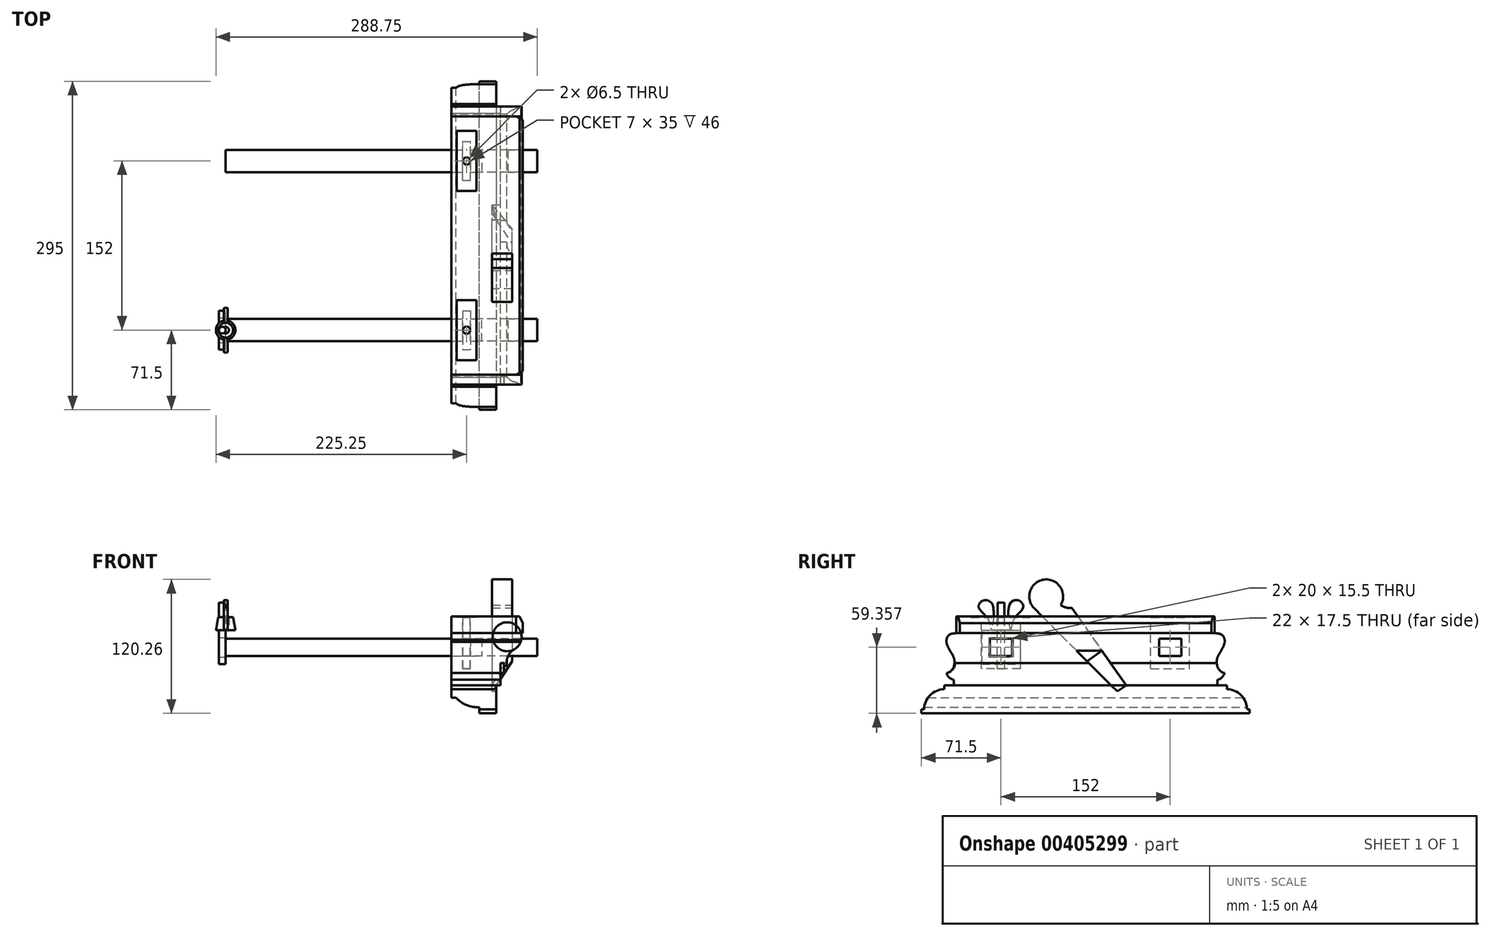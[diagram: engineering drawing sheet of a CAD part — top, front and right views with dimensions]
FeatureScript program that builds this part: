
annotation { "Feature Type Name" : "Feature", "Feature Type Description" : "" }
export const myFeature = defineFeature(function(context is Context, id is Id, definition is map)
    precondition{}
    {
        {
            var Q0;
            Q0=qCreatedBy(makeId("Front.planeOp"),FACE);
            var sketch = newSketch(context, id + "F0", { "sketchPlane" : qUnion([Q0]), "disableImprinting" : false});
            skLineSegment(sketch, "E0", {"start": v(0, 0) * mm, "end": v(0, -42.83) * mm});
            skLineSegment(sketch, "E1", {"start": v(0, -42.83) * mm, "end": v(17, -42.83) * mm});
            skLineSegment(sketch, "E2", {"start": v(17, -42.83) * mm, "end": v(17, -22.83) * mm});
            skLineSegment(sketch, "E3", {"start": v(17, -22.83) * mm, "end": v(20, -22.83) * mm});
            skLineSegment(sketch, "E4", {"start": v(20, -22.83) * mm, "end": v(20, -25.26) * mm});
            skLineSegment(sketch, "E5", {"start": v(20, -25.26) * mm, "end": v(23, -25.26) * mm});
            skLineSegment(sketch, "E6", {"start": v(23, -25.26) * mm, "end": v(35.5, 4.17) * mm});
            skLineSegment(sketch, "E7", {"start": v(35.5, 4.17) * mm, "end": v(37, 4.17) * mm});
            skLineSegment(sketch, "E8", {"start": v(37, 4.17) * mm, "end": v(37, 13.17) * mm});
            skLineSegment(sketch, "E9", {"start": v(37, 13.17) * mm, "end": v(34, 19.17) * mm});
            skLineSegment(sketch, "E10", {"start": v(34, 19.17) * mm, "end": v(0, 19.17) * mm});
            skLineSegment(sketch, "E11", {"start": v(0, 19.17) * mm, "end": v(0, 0) * mm});
            skArc(sketch, "E12", {"start": v(29.25, -10.55) * mm, "mid": v(34.9, -4.26) * mm, "end": v(35.5, 4.17) * mm});
            skArc(sketch, "E13", {"start": v(29.25, -10.55) * mm, "mid": v(23.6, -16.83) * mm, "end": v(23, -25.26) * mm});
            skLineSegment(sketch, "E14.top", {"start": v(17, -55.83) * mm, "end": v(20, -55.83) * mm});
            skLineSegment(sketch, "E14.left", {"start": v(17, -22.83) * mm, "end": v(17, -55.83) * mm});
            skLineSegment(sketch, "E14.right", {"start": v(20, -22.83) * mm, "end": v(20, -55.83) * mm});
            skSolve(sketch);
        }
        {
            var Q0;
            Q0=makeQuery(id+"F0.imprint","IMPRINT",FACE,{"disambiguationData":[TD([[makeQuery(id+"F0.imprint","IMPRINT",EDGE,{"derivedFrom":sQuery(id+"F0.wireOp",EDGE,"E0")}),1.0]])]});
            var Q1;
            {var subQ0=sQuery(id+"F0.wireOp",EDGE,"E12");Q1=makeQuery(id+"F0.imprint","IMPRINT",FACE,{"disambiguationData":[TD([[makeQuery(id+"F0.imprint","IMPRINT",EDGE,{"derivedFrom":subQ0}),1.0]])]});}
            extrude(context, id + "F1", {"entities" : qUnion([Q0, Q1]), "flatOperationType" : FlatOperationType.REMOVE, "offsetDistance" : 25 * mm, "depth" : 250 * mm, "domain" : OperationDomain.MODEL});
        }
        {
            var Q0;
            {var subQ3=sQuery(id+"F0.wireOp",EDGE,"E3");Q0=makeQuery(id+"F0.imprint","IMPRINT",FACE,{"disambiguationData":[TD([[makeQuery(id+"F0.imprint","IMPRINT",EDGE,{"derivedFrom":subQ3}),-1.0]])]});}
            extrude(context, id + "F2", {"entities" : qUnion([Q0]), "flatOperationType" : FlatOperationType.REMOVE, "offsetDistance" : 25 * mm, "depth" : 250 * mm, "domain" : OperationDomain.MODEL});
        }
        {
            var Q0;
            Q0=makeQuery(id+"F1.opExtrude","SWEPT_FACE",FACE,{"disambiguationData":[OSD([sQuery(id+"F0.wireOp",EDGE,"E0"),sQuery(id+"F0.wireOp",EDGE,"E11")])]});
            var sketch = newSketch(context, id + "F3", { "sketchPlane" : qUnion([Q0]), "disableImprinting" : false});
            skLineSegment(sketch, "E15", {"start": v(125, 19.17) * mm, "end": v(125, -42.83) * mm, "construction": true});
            skLineSegment(sketch, "E16", {"start": v(9, 19.17) * mm, "end": v(9, 4.17) * mm});
            skLineSegment(sketch, "E17", {"start": v(9, 4.17) * mm, "end": v(0, -31.83) * mm});
            skLineSegment(sketch, "E18", {"start": v(0, -31.83) * mm, "end": v(6.5, -37.83) * mm});
            skLineSegment(sketch, "E19", {"start": v(6.5, -37.83) * mm, "end": v(6.5, -42.83) * mm});
            skLineSegment(sketch, "E20", {"start": v(6.5, -42.83) * mm, "end": v(6.5, -55.83) * mm});
            skLineSegment(sketch, "E21", {"start": v(6.5, -55.83) * mm, "end": v(0, -55.83) * mm});
            skLineSegment(sketch, "E22", {"start": v(0, -55.83) * mm, "end": v(0, 19.17) * mm});
            skLineSegment(sketch, "E23", {"start": v(0, 19.17) * mm, "end": v(9, 19.17) * mm});
            skArc(sketch, "E24", {"start": v(0, -31.83) * mm, "mid": v(2.45, -35.7) * mm, "end": v(6.5, -37.83) * mm});
            skPoint(sketch, "E25.5.internal.snap0", {"position": v(4.5, -13.83) * mm});
            skFitSpline(sketch, "E25", {"points": [v(9, 4.17) * mm, v(2.4, 2.52) * mm, v(0, -3.64) * mm, v(4.5, -13.83) * mm, v(6.98, -19.62) * mm, v(6.63, -25.76) * mm, v(4.5, -29.45) * mm, v(2.76, -30.82) * mm, v(0, -31.83) * mm], "startDerivative": vector(-67.53, -10.91) * mm, "endDerivative": vector(-24.37, -5.27) * mm});
            skLineSegment(sketch, "E26.MirrorCS", {"start": v(250, -31.83) * mm, "end": v(243.5, -37.83) * mm});
            skLineSegment(sketch, "E27.MirrorCS", {"start": v(243.5, -37.83) * mm, "end": v(243.5, -42.83) * mm});
            skLineSegment(sketch, "E28.MirrorCS", {"start": v(243.5, -55.83) * mm, "end": v(250, -55.83) * mm});
            skArc(sketch, "E29.MirrorCS", {"start": v(250, -31.83) * mm, "mid": v(247.55, -35.7) * mm, "end": v(243.5, -37.83) * mm});
            skFitSpline(sketch, "E30.MirrorCS", {"points": [v(241, 4.17) * mm, v(247.6, 2.52) * mm, v(250, -3.64) * mm, v(245.5, -13.83) * mm, v(243.02, -19.62) * mm, v(243.37, -25.76) * mm, v(245.5, -29.45) * mm, v(247.24, -30.82) * mm, v(250, -31.83) * mm], "startDerivative": vector(67.53, -10.91) * mm, "endDerivative": vector(24.37, -5.27) * mm});
            skLineSegment(sketch, "E31.MirrorCS", {"start": v(241, 19.17) * mm, "end": v(241, 4.17) * mm});
            skLineSegment(sketch, "E32.MirrorCS", {"start": v(241, 4.17) * mm, "end": v(250, -31.83) * mm});
            skLineSegment(sketch, "E33.MirrorCS", {"start": v(243.5, -42.83) * mm, "end": v(243.5, -55.83) * mm});
            skLineSegment(sketch, "E34.MirrorCS", {"start": v(250, 19.17) * mm, "end": v(241, 19.17) * mm});
            skLineSegment(sketch, "E35.MirrorCS", {"start": v(250, -55.83) * mm, "end": v(250, 19.17) * mm});
            skSolve(sketch);
        }
        {
            var Q0;
            {var subQ0=sQuery(id+"F3.wireOp",EDGE,"E16");Q0=makeQuery(id+"F3.imprint","IMPRINT",FACE,{"disambiguationData":[TD([[makeQuery(id+"F3.imprint","IMPRINT",EDGE,{"derivedFrom":subQ0}),-1.0]])]});}
            var Q1;
            {var subQ0=sQuery(id+"F3.wireOp",EDGE,"E25");var subQ1=sQuery(id+"F3.wireOp",EDGE,"E17");var subQ3=makeQuery(id+"F3.imprint","INTERSECT",VERTEX,{"derivedFrom":[subQ1,subQ0]});Q1=makeQuery(id+"F3.imprint","IMPRINT",FACE,{"disambiguationData":[TD([[makeQuery(id+"F3.imprint","IMPRINT",EDGE,{"disambiguationData":[TD([[subQ3,-1.0]])],"derivedFrom":subQ1}),1.0]])]});}
            var Q2;
            {var subQ0=sQuery(id+"F3.wireOp",EDGE,"E25");var subQ1=sQuery(id+"F3.wireOp",EDGE,"E22");var subQ5=makeQuery(id+"F3.imprint","INTERSECT",VERTEX,{"disambiguationData":[OD(1.0)],"derivedFrom":[subQ1,subQ0]});Q2=makeQuery(id+"F3.imprint","IMPRINT",FACE,{"disambiguationData":[TD([[makeQuery(id+"F3.imprint","IMPRINT",EDGE,{"disambiguationData":[TD([[subQ5,-1.0]])],"derivedFrom":subQ0}),-1.0]])]});}
            var Q3;
            {var subQ0=sQuery(id+"F3.wireOp",EDGE,"E19");Q3=makeQuery(id+"F3.imprint","IMPRINT",FACE,{"disambiguationData":[TD([[makeQuery(id+"F3.imprint","IMPRINT",EDGE,{"derivedFrom":subQ0}),-1.0]])]});}
            var Q4;
            {var subQ0=sQuery(id+"F3.wireOp",EDGE,"E20");Q4=makeQuery(id+"F3.imprint","IMPRINT",FACE,{"disambiguationData":[TD([[makeQuery(id+"F3.imprint","IMPRINT",EDGE,{"derivedFrom":subQ0}),-1.0]])]});}
            var Q5;
            {var subQ0=sQuery(id+"F3.wireOp",EDGE,"E31.MirrorCS");Q5=makeQuery(id+"F3.imprint","IMPRINT",FACE,{"disambiguationData":[TD([[makeQuery(id+"F3.imprint","IMPRINT",EDGE,{"derivedFrom":subQ0}),1.0]])]});}
            var Q6;
            {var subQ0=sQuery(id+"F3.wireOp",EDGE,"E35.MirrorCS");var subQ1=sQuery(id+"F3.wireOp",EDGE,"E30.MirrorCS");var subQ2=makeQuery(id+"F3.imprint","INTERSECT",VERTEX,{"disambiguationData":[OD(1.0)],"derivedFrom":[subQ1,subQ0]});Q6=makeQuery(id+"F3.imprint","IMPRINT",FACE,{"disambiguationData":[TD([[makeQuery(id+"F3.imprint","IMPRINT",EDGE,{"disambiguationData":[TD([[subQ2,-1.0]])],"derivedFrom":subQ1}),1.0]])]});}
            var Q7;
            {var subQ0=sQuery(id+"F3.wireOp",EDGE,"E32.MirrorCS");var subQ1=sQuery(id+"F3.wireOp",EDGE,"E30.MirrorCS");var subQ3=makeQuery(id+"F3.imprint","INTERSECT",VERTEX,{"derivedFrom":[subQ1,subQ0]});Q7=makeQuery(id+"F3.imprint","IMPRINT",FACE,{"disambiguationData":[TD([[makeQuery(id+"F3.imprint","IMPRINT",EDGE,{"disambiguationData":[TD([[subQ3,-1.0]])],"derivedFrom":subQ1}),1.0]])]});}
            var Q8;
            {var subQ0=sQuery(id+"F3.wireOp",EDGE,"E27.MirrorCS");Q8=makeQuery(id+"F3.imprint","IMPRINT",FACE,{"disambiguationData":[TD([[makeQuery(id+"F3.imprint","IMPRINT",EDGE,{"derivedFrom":subQ0}),1.0]])]});}
            var Q9;
            {var subQ0=sQuery(id+"F3.wireOp",EDGE,"E28.MirrorCS");Q9=makeQuery(id+"F3.imprint","IMPRINT",FACE,{"disambiguationData":[TD([[makeQuery(id+"F3.imprint","IMPRINT",EDGE,{"derivedFrom":subQ0}),1.0]])]});}
            extrude(context, id + "F4", {"entities" : qUnion([Q0, Q1, Q2, Q3, Q4, Q5, Q6, Q7, Q8, Q9]), "operationType" : NewBodyOperationType.REMOVE, "endBound" : BoundingType.THROUGH_ALL, "oppositeDirection" : true, "depth" : 25 * mm});
        }
        {
            var Q0;
            Q0=makeQuery(id+"F2.opExtrude","SWEPT_FACE",FACE,{"disambiguationData":[OSD([sQuery(id+"F0.wireOp",EDGE,"E14.left")])]});
            var sketch = newSketch(context, id + "F5", { "sketchPlane" : qUnion([Q0])});
            skFitSpline(sketch, "E36.0", {"points": [v(0, -31.83) * mm, v(0.74, -31.67) * mm, v(2.94, -30.89) * mm, v(4.62, -29.53) * mm, v(7.17, -25.8) * mm, v(7.43, -19.25) * mm, v(4.68, -13.85) * mm, v(-1.65, -4.08) * mm, v(2, 3.76) * mm, v(5.87, 3.66) * mm, v(9, 4.17) * mm]});
            skArc(sketch, "E37.0", {"start": v(6.5, -37.83) * mm, "mid": v(2.45, -35.7) * mm, "end": v(0, -31.83) * mm});
            skLineSegment(sketch, "E38.0", {"start": v(6.5, -42.83) * mm, "end": v(6.5, -37.83) * mm});
            skLineSegment(sketch, "E39", {"start": v(7.16, -22.83) * mm, "end": v(0, -22.83) * mm});
            skLineSegment(sketch, "E40", {"start": v(0, -22.83) * mm, "end": v(0, -55.83) * mm});
            skLineSegment(sketch, "E41", {"start": v(0, -55.83) * mm, "end": v(6.5, -55.83) * mm});
            skLineSegment(sketch, "E42", {"start": v(6.5, -55.83) * mm, "end": v(6.5, -42.83) * mm});
            skLineSegment(sketch, "E43", {"start": v(125, -22.83) * mm, "end": v(125, -55.83) * mm, "construction": true});
            skLineSegment(sketch, "E44.MirrorCS", {"start": v(243.5, -42.83) * mm, "end": v(243.5, -37.83) * mm});
            skLineSegment(sketch, "E45.MirrorCS", {"start": v(242.84, -22.83) * mm, "end": v(250, -22.83) * mm});
            skLineSegment(sketch, "E46.MirrorCS", {"start": v(250, -55.83) * mm, "end": v(243.5, -55.83) * mm});
            skArc(sketch, "E47.MirrorCS", {"start": v(243.5, -37.83) * mm, "mid": v(247.55, -35.7) * mm, "end": v(250, -31.83) * mm});
            skLineSegment(sketch, "E48.MirrorCS", {"start": v(243.5, -55.83) * mm, "end": v(243.5, -42.83) * mm});
            skLineSegment(sketch, "E49.MirrorCS", {"start": v(250, -22.83) * mm, "end": v(250, -55.83) * mm});
            skFitSpline(sketch, "E50.0", {"points": [v(250, -31.83) * mm, v(249.26, -31.67) * mm, v(247.06, -30.89) * mm, v(245.38, -29.53) * mm, v(242.83, -25.8) * mm, v(242.57, -19.25) * mm, v(245.32, -13.85) * mm, v(251.65, -4.08) * mm, v(248, 3.76) * mm, v(244.13, 3.66) * mm, v(241, 4.17) * mm]});
            skSolve(sketch);
        }
        {
            var Q0;
            {var subQ0=sQuery(id+"F5.wireOp",EDGE,"E45.MirrorCS");Q0=makeQuery(id+"F5.imprint","IMPRINT",FACE,{"disambiguationData":[TD([[makeQuery(id+"F5.imprint","IMPRINT",EDGE,{"derivedFrom":subQ0}),1.0]])]});}
            var Q1;
            Q1=makeQuery(id+"F5.imprint","IMPRINT",FACE,{"disambiguationData":[TD([[makeQuery(id+"F5.imprint","IMPRINT",EDGE,{"derivedFrom":sQuery(id+"F5.wireOp",EDGE,"E44.MirrorCS")}),-1.0]])]});
            var Q2;
            {var subQ0=sQuery(id+"F5.wireOp",EDGE,"E36.0");Q2=makeQuery(id+"F5.imprint","IMPRINT",FACE,{"disambiguationData":[TD([[makeQuery(id+"F5.imprint","IMPRINT",EDGE,{"derivedFrom":subQ0}),1.0]])]});}
            var Q3;
            {var subQ2=sQuery(id+"F5.wireOp",EDGE,"E37.0");Q3=makeQuery(id+"F5.imprint","IMPRINT",FACE,{"disambiguationData":[TD([[makeQuery(id+"F5.imprint","IMPRINT",EDGE,{"derivedFrom":subQ2}),1.0]])]});}
            extrude(context, id + "F6", {"entities" : qUnion([Q0, Q1, Q2, Q3]), "operationType" : NewBodyOperationType.REMOVE, "endBound" : BoundingType.THROUGH_ALL, "oppositeDirection" : true, "depth" : 25 * mm});
        }
        {
            var Q0;
            Q0=makeQuery(id+"F1.opExtrude","SWEPT_FACE",FACE,{"disambiguationData":[OSD([sQuery(id+"F0.wireOp",EDGE,"E10")])]});
            var sketch = newSketch(context, id + "F7", { "sketchPlane" : qUnion([Q0])});
            skLineSegment(sketch, "E51", {"start": v(34, -9) * mm, "end": v(31, -9) * mm});
            skLineSegment(sketch, "E52", {"start": v(31, -9) * mm, "end": v(37, -12) * mm});
            skLineSegment(sketch, "E53", {"start": v(37, -12) * mm, "end": v(37, -9) * mm});
            skLineSegment(sketch, "E54", {"start": v(37, -9) * mm, "end": v(34, -9) * mm});
            skLineSegment(sketch, "E55", {"start": v(0, -125) * mm, "end": v(34, -125) * mm, "construction": true});
            skLineSegment(sketch, "E56.MirrorCS", {"start": v(37, -238) * mm, "end": v(37, -241) * mm});
            skLineSegment(sketch, "E57.MirrorCS", {"start": v(31, -241) * mm, "end": v(37, -238) * mm});
            skLineSegment(sketch, "E58.MirrorCS", {"start": v(34, -241) * mm, "end": v(31, -241) * mm});
            skLineSegment(sketch, "E59.MirrorCS", {"start": v(37, -241) * mm, "end": v(34, -241) * mm});
            skSolve(sketch);
        }
        {
            var Q0;
            {var subQ0=sQuery(id+"F7.wireOp",EDGE,"E51");Q0=makeQuery(id+"F7.imprint","IMPRINT",FACE,{"disambiguationData":[TD([[makeQuery(id+"F7.imprint","IMPRINT",EDGE,{"derivedFrom":subQ0}),1.0]])]});}
            var Q1;
            {var subQ0=sQuery(id+"F7.wireOp",EDGE,"E53");Q1=makeQuery(id+"F7.imprint","IMPRINT",FACE,{"disambiguationData":[TD([[makeQuery(id+"F7.imprint","IMPRINT",EDGE,{"derivedFrom":subQ0}),1.0]])]});}
            var Q2;
            Q2=makeQuery(id+"F1.opExtrude","SWEPT_FACE",FACE,{"disambiguationData":[OSD([sQuery(id+"F0.wireOp",EDGE,"E7")])]});
            extrude(context, id + "F8", {"entities" : qUnion([Q0, Q1]), "operationType" : NewBodyOperationType.REMOVE, "endBound" : BoundingType.UP_TO_SURFACE, "oppositeDirection" : true, "endBoundEntityFace" : qUnion([Q2]), "depth" : 25 * mm});
        }
        {
            var Q0;
            {var subQ0=sQuery(id+"F7.wireOp",EDGE,"E56.MirrorCS");Q0=makeQuery(id+"F7.imprint","IMPRINT",FACE,{"disambiguationData":[TD([[makeQuery(id+"F7.imprint","IMPRINT",EDGE,{"derivedFrom":subQ0}),-1.0]])]});}
            var Q1;
            {var subQ0=sQuery(id+"F7.wireOp",EDGE,"E58.MirrorCS");Q1=makeQuery(id+"F7.imprint","IMPRINT",FACE,{"disambiguationData":[TD([[makeQuery(id+"F7.imprint","IMPRINT",EDGE,{"derivedFrom":subQ0}),-1.0]])]});}
            var Q2;
            Q2=makeQuery(id+"F1.opExtrude","SWEPT_FACE",FACE,{"disambiguationData":[OSD([sQuery(id+"F0.wireOp",EDGE,"E7")])]});
            extrude(context, id + "F9", {"entities" : qUnion([Q0, Q1]), "operationType" : NewBodyOperationType.REMOVE, "endBound" : BoundingType.UP_TO_SURFACE, "oppositeDirection" : true, "endBoundEntityFace" : qUnion([Q2]), "depth" : 25 * mm});
        }
        {
            var Q0;
            Q0=makeQuery(id+"F1.opExtrude","SWEPT_FACE",FACE,{"disambiguationData":[OSD([sQuery(id+"F0.wireOp",EDGE,"E0"),sQuery(id+"F0.wireOp",EDGE,"E11")])]});
            var sketch = newSketch(context, id + "F10", { "sketchPlane" : qUnion([Q0])});
            skLineSegment(sketch, "E60.bottom", {"start": v(39, -0.83) * mm, "end": v(59, -0.83) * mm});
            skLineSegment(sketch, "E60.top", {"start": v(39, -16.33) * mm, "end": v(59, -16.33) * mm});
            skLineSegment(sketch, "E60.left", {"start": v(39, -0.83) * mm, "end": v(39, -16.33) * mm});
            skLineSegment(sketch, "E60.right", {"start": v(59, -0.83) * mm, "end": v(59, -16.33) * mm});
            skLineSegment(sketch, "E61", {"start": v(125, 19.17) * mm, "end": v(125, -42.83) * mm, "construction": true});
            skLineSegment(sketch, "E62.MirrorCS", {"start": v(211, -0.83) * mm, "end": v(191, -0.83) * mm});
            skLineSegment(sketch, "E63.MirrorCS", {"start": v(211, -16.33) * mm, "end": v(191, -16.33) * mm});
            skLineSegment(sketch, "E64.MirrorCS", {"start": v(211, -0.83) * mm, "end": v(211, -16.33) * mm});
            skLineSegment(sketch, "E65.MirrorCS", {"start": v(191, -0.83) * mm, "end": v(191, -16.33) * mm});
            skSolve(sketch);
        }
        {
            var Q0;
            Q0=makeQuery(id+"F10.imprint","IMPRINT",FACE,{"disambiguationData":[TD([[makeQuery(id+"F10.imprint","IMPRINT",EDGE,{"derivedFrom":sQuery(id+"F10.wireOp",EDGE,"E60.bottom")}),-1.0]])]});
            var Q1;
            Q1=makeQuery(id+"F10.imprint","IMPRINT",FACE,{"disambiguationData":[TD([[makeQuery(id+"F10.imprint","IMPRINT",EDGE,{"derivedFrom":sQuery(id+"F10.wireOp",EDGE,"E62.MirrorCS")}),1.0]])]});
            var Q2;
            Q2=makeQuery(id+"F1.opExtrude","SWEPT_FACE",FACE,{"disambiguationData":[OSD([sQuery(id+"F0.wireOp",EDGE,"E12")])]});
            extrude(context, id + "F11", {"entities" : qUnion([Q0, Q1]), "operationType" : NewBodyOperationType.REMOVE, "endBound" : BoundingType.UP_TO_NEXT, "oppositeDirection" : true, "endBoundEntityFace" : qUnion([Q2]), "depth" : 25 * mm});
        }
        {
            var Q0;
            Q0=makeQuery(id+"F10.imprint","IMPRINT",FACE,{"disambiguationData":[TD([[makeQuery(id+"F10.imprint","IMPRINT",EDGE,{"derivedFrom":sQuery(id+"F10.wireOp",EDGE,"E62.MirrorCS")}),1.0]])]});
            var Q1;
            Q1=makeQuery(id+"F10.imprint","IMPRINT",FACE,{"disambiguationData":[TD([[makeQuery(id+"F10.imprint","IMPRINT",EDGE,{"derivedFrom":sQuery(id+"F10.wireOp",EDGE,"E60.bottom")}),-1.0]])]});
            var Q2;
            Q2=makeQuery(id+"F1.opExtrude","SWEPT_FACE",FACE,{"disambiguationData":[OSD([sQuery(id+"F0.wireOp",EDGE,"E13")])]});
            extrude(context, id + "F12", {"entities" : qUnion([Q0, Q1]), "oppositeDirection" : true, "endBoundEntityFace" : qUnion([Q2]), "depth" : 50 * mm});
        }
        {
            var Q0;
            Q0=makeQuery(id+"F10.imprint","IMPRINT",FACE,{"disambiguationData":[TD([[makeQuery(id+"F10.imprint","IMPRINT",EDGE,{"derivedFrom":sQuery(id+"F10.wireOp",EDGE,"E62.MirrorCS")}),1.0]])]});
            var Q1;
            Q1=makeQuery(id+"F10.imprint","IMPRINT",FACE,{"disambiguationData":[TD([[makeQuery(id+"F10.imprint","IMPRINT",EDGE,{"derivedFrom":sQuery(id+"F10.wireOp",EDGE,"E60.bottom")}),-1.0]])]});
            extrude(context, id + "F13", {"entities" : qUnion([Q0, Q1]), "depth" : 230 * mm});
        }
        {
            var Q0;
            Q0=makeQuery(id+"F12.opExtrude","SWEPT_FACE",FACE,{"disambiguationData":[OSD([sQuery(id+"F10.wireOp",EDGE,"E60.left")])]});
            var sketch = newSketch(context, id + "F14", { "sketchPlane" : qUnion([Q0])});
            skArc(sketch, "E66.0", {"start": v(-29.25, -10.55) * mm, "mid": v(-33.7, -6.47) * mm, "end": v(-35.83, -0.83) * mm});
            skArc(sketch, "E67.0", {"start": v(-29.25, -10.55) * mm, "mid": v(-26.08, -13.01) * mm, "end": v(-23.82, -16.33) * mm});
            skLineSegment(sketch, "E68.0", {"start": v(-50, -16.33) * mm, "end": v(0, -16.33) * mm});
            skLineSegment(sketch, "E69.0", {"start": v(-50, -0.83) * mm, "end": v(-50, -16.33) * mm});
            skLineSegment(sketch, "E70.0", {"start": v(-50, -0.83) * mm, "end": v(0, -0.83) * mm});
            skSolve(sketch);
        }
        {
            var Q0;
            {var subQ3=sQuery(id+"F14.wireOp",EDGE,"E66.0");Q0=makeQuery(id+"F14.imprint","IMPRINT",FACE,{"disambiguationData":[TD([[makeQuery(id+"F14.imprint","IMPRINT",EDGE,{"derivedFrom":subQ3}),1.0]])]});}
            var Q1;
            Q1=makeQuery(id+"F12.opExtrude","SWEPT_FACE",FACE,{"disambiguationData":[OSD([sQuery(id+"F10.wireOp",EDGE,"E60.right")])]});
            extrude(context, id + "F15", {"entities" : qUnion([Q0]), "operationType" : NewBodyOperationType.REMOVE, "endBound" : BoundingType.UP_TO_SURFACE, "oppositeDirection" : true, "endBoundEntityFace" : qUnion([Q1]), "depth" : 25 * mm});
        }
        {
            var Q0;
            Q0=makeQuery(id+"F12.opExtrude","SWEPT_FACE",FACE,{"disambiguationData":[OSD([sQuery(id+"F10.wireOp",EDGE,"E65.MirrorCS")])]});
            var sketch = newSketch(context, id + "F16", { "sketchPlane" : qUnion([Q0])});
            skArc(sketch, "E71.0", {"start": v(-29.25, -10.55) * mm, "mid": v(-33.7, -6.47) * mm, "end": v(-35.83, -0.83) * mm});
            skArc(sketch, "E72.0", {"start": v(-29.25, -10.55) * mm, "mid": v(-26.08, -13.01) * mm, "end": v(-23.82, -16.33) * mm});
            skLineSegment(sketch, "E73.0", {"start": v(-50, -16.33) * mm, "end": v(0, -16.33) * mm});
            skLineSegment(sketch, "E74.0", {"start": v(-50, -0.83) * mm, "end": v(-50, -16.33) * mm});
            skLineSegment(sketch, "E75.0", {"start": v(-50, -0.83) * mm, "end": v(0, -0.83) * mm});
            skSolve(sketch);
        }
        {
            var Q0;
            {var subQ3=sQuery(id+"F16.wireOp",EDGE,"E71.0");Q0=makeQuery(id+"F16.imprint","IMPRINT",FACE,{"disambiguationData":[TD([[makeQuery(id+"F16.imprint","IMPRINT",EDGE,{"derivedFrom":subQ3}),1.0]])]});}
            var Q1;
            Q1=makeQuery(id+"F12.opExtrude","SWEPT_FACE",FACE,{"disambiguationData":[OSD([sQuery(id+"F10.wireOp",EDGE,"E64.MirrorCS")])]});
            extrude(context, id + "F17", {"entities" : qUnion([Q0]), "operationType" : NewBodyOperationType.REMOVE, "endBound" : BoundingType.UP_TO_SURFACE, "oppositeDirection" : true, "endBoundEntityFace" : qUnion([Q1]), "depth" : 25 * mm});
        }
        {
            var Q0;
            Q0=makeQuery(id+"F13.opExtrude","SWEPT_BODY",BODY,{"disambiguationData":[OSD([sQuery(id+"F10.wireOp",EDGE,"E62.MirrorCS"),sQuery(id+"F10.wireOp",EDGE,"E63.MirrorCS"),sQuery(id+"F10.wireOp",EDGE,"E64.MirrorCS"),sQuery(id+"F10.wireOp",EDGE,"E65.MirrorCS")])]});
            var Q1;
            Q1=makeQuery(id+"F12.opExtrude","SWEPT_BODY",BODY,{"disambiguationData":[OSD([sQuery(id+"F10.wireOp",EDGE,"E62.MirrorCS"),sQuery(id+"F10.wireOp",EDGE,"E63.MirrorCS"),sQuery(id+"F10.wireOp",EDGE,"E64.MirrorCS"),sQuery(id+"F10.wireOp",EDGE,"E65.MirrorCS")])]});
            booleanBodies(context, id + "F18", {"operationType" : BooleanOperationType.UNION, "tools" : qUnion([Q0, Q1])});
        }
        {
            var Q0;
            Q0=makeQuery(id+"F1.opExtrude","SWEPT_FACE",FACE,{"disambiguationData":[OSD([sQuery(id+"F0.wireOp",EDGE,"E0"),sQuery(id+"F0.wireOp",EDGE,"E11")])]});
            cPlane(context, id + "F19", {"entities" : qUnion([Q0]), "cplaneType" : CPlaneType.OFFSET, "offset" : 18.5 * mm, "oppositeDirection" : true, "width" : 150 * mm, "height" : 150 * mm});
        }
        {
            var Q0;
            Q0=qCreatedBy(id+"F19.planeOp",FACE);
            var sketch = newSketch(context, id + "F20", { "sketchPlane" : qUnion([Q0])});
            skLineSegment(sketch, "E76.0", {"start": v(241, 19.17) * mm, "end": v(9, 19.17) * mm});
            skLineSegment(sketch, "E77.0", {"start": v(243.5, -55.83) * mm, "end": v(6.5, -55.83) * mm});
            skLineSegment(sketch, "E78", {"start": v(164, 19.17) * mm, "end": v(89, -55.83) * mm});
            skLineSegment(sketch, "E79", {"start": v(132, 19.17) * mm, "end": v(79.48, -55.83) * mm});
            skLineSegment(sketch, "E80", {"start": v(132, 19.17) * mm, "end": v(137.36, 26.82) * mm});
            skArc(sketch, "E81", {"start": v(137.36, 26.82) * mm, "mid": v(142.56, 27.1) * mm, "end": v(147.35, 29.16) * mm});
            skLineSegment(sketch, "E82", {"start": v(164, 19.17) * mm, "end": v(171.14, 26.3) * mm});
            skArc(sketch, "E83", {"start": v(171.14, 26.3) * mm, "mid": v(162.18, 52.2) * mm, "end": v(147.35, 29.16) * mm});
            skLineSegment(sketch, "E84", {"start": v(88.59, -42.83) * mm, "end": v(102, -42.83) * mm});
            skSolve(sketch);
        }
        {
            var Q0;
            {var subQ0=sQuery(id+"F20.wireOp",EDGE,"E78");Q0=makeQuery(id+"F20.imprint","IMPRINT",FACE,{"disambiguationData":[TD([[makeQuery(id+"F20.imprint","IMPRINT",EDGE,{"derivedFrom":subQ0}),-1.0]])]});}
            extrude(context, id + "F21", {"entities" : qUnion([Q0]), "operationType" : NewBodyOperationType.REMOVE, "oppositeDirection" : true, "depth" : 18 * mm, "symmetric" : true});
        }
        {
            var Q0;
            Q0=makeQuery(id+"F1.opExtrude","SWEPT_FACE",FACE,{"disambiguationData":[OSD([sQuery(id+"F0.wireOp",EDGE,"E0"),sQuery(id+"F0.wireOp",EDGE,"E11")])]});
            extrude(context, id + "F22", {"entities" : qUnion([Q0]), "depth" : 27 * mm});
        }
        {
            var Q0;
            Q0=makeQuery(id+"F22.opExtrude","CAP_FACE",FACE,{"disambiguationData":[OSD([sQuery(id+"F0.wireOp",EDGE,"E0"),sQuery(id+"F0.wireOp",EDGE,"E11")])],"isStart":false});
            var sketch = newSketch(context, id + "F23", { "sketchPlane" : qUnion([Q0])});
            skLineSegment(sketch, "E85", {"start": v(6.5, -42.83) * mm, "end": v(-2, -42.83) * mm});
            skLineSegment(sketch, "E86", {"start": v(-2, -42.83) * mm, "end": v(-2, -46.33) * mm});
            skLineSegment(sketch, "E87", {"start": v(-20, -64.33) * mm, "end": v(-22.5, -64.33) * mm});
            skLineSegment(sketch, "E88", {"start": v(-22.5, -64.33) * mm, "end": v(-22.5, -67.94) * mm});
            skArc(sketch, "E89", {"start": v(-2, -46.33) * mm, "mid": v(-14.73, -51.6) * mm, "end": v(-20, -64.33) * mm});
            skLineSegment(sketch, "E90", {"start": v(125, 19.17) * mm, "end": v(125, -42.83) * mm, "construction": true});
            skLineSegment(sketch, "E91.MirrorCS", {"start": v(270, -64.33) * mm, "end": v(272.5, -64.33) * mm});
            skLineSegment(sketch, "E92.MirrorCS", {"start": v(252, -42.83) * mm, "end": v(252, -46.33) * mm});
            skLineSegment(sketch, "E93.MirrorCS", {"start": v(243.5, -42.83) * mm, "end": v(252, -42.83) * mm});
            skArc(sketch, "E94.MirrorCS", {"start": v(252, -46.33) * mm, "mid": v(264.73, -51.6) * mm, "end": v(270, -64.33) * mm});
            skLineSegment(sketch, "E95.MirrorCS", {"start": v(272.5, -64.33) * mm, "end": v(272.5, -67.94) * mm});
            skLineSegment(sketch, "E96", {"start": v(-22.5, -67.94) * mm, "end": v(272.5, -67.94) * mm});
            skLineSegment(sketch, "E97", {"start": v(243.5, -42.83) * mm, "end": v(6.5, -42.83) * mm});
            skSolve(sketch);
        }
        {
            var Q0;
            Q0=makeQuery(id+"F23.imprint","IMPRINT",FACE,{"disambiguationData":[TD([[makeQuery(id+"F23.imprint","IMPRINT",EDGE,{"derivedFrom":sQuery(id+"F23.wireOp",EDGE,"E85")}),1.0]])]});
            extrude(context, id + "F24", {"entities" : qUnion([Q0]), "operationType" : NewBodyOperationType.ADD, "oppositeDirection" : true, "depth" : 40 * mm});
        }
        {
            var Q0;
            Q0=makeQuery(id+"F24.opExtrude","SWEPT_FACE",FACE,{"disambiguationData":[OSD([sQuery(id+"F23.wireOp",EDGE,"E88")])]});
            var sketch = newSketch(context, id + "F25", { "sketchPlane" : qUnion([Q0])});
            skLineSegment(sketch, "E98", {"start": v(2, -67.94) * mm, "end": v(2, -62.44) * mm});
            skLineSegment(sketch, "E99", {"start": v(23, -53.94) * mm, "end": v(27, -53.94) * mm});
            skLineSegment(sketch, "E100", {"start": v(2, -67.94) * mm, "end": v(27, -67.94) * mm});
            skLineSegment(sketch, "E101", {"start": v(27, -67.94) * mm, "end": v(27, -53.94) * mm});
            skArc(sketch, "E102", {"start": v(2, -62.44) * mm, "mid": v(13.47, -60.6) * mm, "end": v(23, -53.94) * mm});
            skSolve(sketch);
        }
        {
            var Q0;
            {var subQ3=sQuery(id+"F25.wireOp",EDGE,"E99");Q0=makeQuery(id+"F25.imprint","IMPRINT",FACE,{"disambiguationData":[TD([[makeQuery(id+"F25.imprint","IMPRINT",EDGE,{"derivedFrom":subQ3}),-1.0]])]});}
            var Q1;
            {var subQ0=sQuery(id+"F25.wireOp",EDGE,"E100");Q1=makeQuery(id+"F25.imprint","IMPRINT",FACE,{"disambiguationData":[TD([[makeQuery(id+"F25.imprint","IMPRINT",EDGE,{"derivedFrom":subQ0}),1.0]])]});}
            extrude(context, id + "F26", {"entities" : qUnion([Q0, Q1]), "operationType" : NewBodyOperationType.REMOVE, "endBound" : BoundingType.THROUGH_ALL, "oppositeDirection" : true, "depth" : 25 * mm});
        }
        {
            var Q0;
            {var subQ5=sQuery(id+"F20.wireOp",EDGE,"E84");Q0=makeQuery(id+"F20.imprint","IMPRINT",FACE,{"disambiguationData":[TD([[makeQuery(id+"F20.imprint","IMPRINT",EDGE,{"derivedFrom":subQ5}),1.0]])]});}
            var Q1;
            {var subQ1=sQuery(id+"F20.wireOp",EDGE,"E80");Q1=makeQuery(id+"F20.imprint","IMPRINT",FACE,{"disambiguationData":[TD([[makeQuery(id+"F20.imprint","IMPRINT",EDGE,{"derivedFrom":subQ1}),-1.0]])]});}
            extrude(context, id + "F27", {"entities" : qUnion([Q0, Q1]), "depth" : 18 * mm, "symmetric" : true});
        }
        {
            var Q0;
            Q0=makeQuery(id+"F27.opExtrude","SWEPT_FACE",FACE,{"disambiguationData":[OSD([sQuery(id+"F20.wireOp",EDGE,"E79"),sQuery(id+"F20.wireOp",EDGE,"E80")])]});
            var sketch = newSketch(context, id + "F28", { "sketchPlane" : qUnion([Q0])});
            skLineSegment(sketch, "E103", {"start": v(-9.5, 15.72) * mm, "end": v(-27.5, 53.72) * mm});
            skLineSegment(sketch, "E104", {"start": v(-27.5, 53.72) * mm, "end": v(-27.5, 15.72) * mm});
            skLineSegment(sketch, "E105", {"start": v(-27.5, 15.72) * mm, "end": v(-9.5, 15.72) * mm});
            skSolve(sketch);
        }
        {
            var Q0;
            Q0=makeQuery(id+"F28.imprint","IMPRINT",FACE,{"disambiguationData":[TD([[makeQuery(id+"F28.imprint","IMPRINT",EDGE,{"derivedFrom":sQuery(id+"F28.wireOp",EDGE,"E103")}),1.0]])]});
            var Q1;
            Q1=makeQuery(id+"F27.opExtrude","SWEPT_FACE",FACE,{"disambiguationData":[OSD([sQuery(id+"F20.wireOp",EDGE,"E78"),sQuery(id+"F20.wireOp",EDGE,"E82")])]});
            extrude(context, id + "F29", {"entities" : qUnion([Q0]), "operationType" : NewBodyOperationType.REMOVE, "endBound" : BoundingType.UP_TO_SURFACE, "oppositeDirection" : true, "endBoundEntityFace" : qUnion([Q1]), "depth" : 25 * mm});
        }
        {
            var Q0;
            Q0=makeQuery(id+"F22.opExtrude","SWEPT_FACE",FACE,{"disambiguationData":[OSD([sQuery(id+"F0.wireOp",EDGE,"E10"),sQuery(id+"F0.wireOp",EDGE,"E11")])]});
            var sketch = newSketch(context, id + "F30", { "sketchPlane" : qUnion([Q0])});
            skLineSegment(sketch, "E106", {"start": v(0, -125) * mm, "end": v(-27, -125) * mm, "construction": true});
            skLineSegment(sketch, "E107.bottom", {"start": v(-4.5, -22) * mm, "end": v(-22.5, -22) * mm});
            skLineSegment(sketch, "E107.top", {"start": v(-4.5, -76) * mm, "end": v(-22.5, -76) * mm});
            skLineSegment(sketch, "E107.left", {"start": v(-4.5, -22) * mm, "end": v(-4.5, -76) * mm});
            skLineSegment(sketch, "E107.right", {"start": v(-22.5, -22) * mm, "end": v(-22.5, -76) * mm});
            skLineSegment(sketch, "E108", {"start": v(-4.5, -49) * mm, "end": v(-22.5, -49) * mm, "construction": true});
            skLineSegment(sketch, "E109", {"start": v(-4.5, -22) * mm, "end": v(0, -22) * mm, "construction": true});
            skLineSegment(sketch, "E110", {"start": v(-22.5, -22) * mm, "end": v(-27, -22) * mm, "construction": true});
            skLineSegment(sketch, "E111.bottom", {"start": v(-17, -66.5) * mm, "end": v(-10, -66.5) * mm});
            skLineSegment(sketch, "E111.top", {"start": v(-17, -31.5) * mm, "end": v(-10, -31.5) * mm});
            skLineSegment(sketch, "E111.left", {"start": v(-17, -66.5) * mm, "end": v(-17, -31.5) * mm});
            skLineSegment(sketch, "E111.right", {"start": v(-10, -66.5) * mm, "end": v(-10, -31.5) * mm});
            skPoint(sketch, "E111.middle", {"position": v(-13.5, -49) * mm});
            skLineSegment(sketch, "E112.MirrorCS", {"start": v(-4.5, -228) * mm, "end": v(0, -228) * mm, "construction": true});
            skLineSegment(sketch, "E113.MirrorCS", {"start": v(-22.5, -228) * mm, "end": v(-27, -228) * mm, "construction": true});
            skLineSegment(sketch, "E114.MirrorCS", {"start": v(-4.5, -228) * mm, "end": v(-4.5, -174) * mm});
            skLineSegment(sketch, "E115.MirrorCS", {"start": v(-22.5, -228) * mm, "end": v(-22.5, -174) * mm});
            skLineSegment(sketch, "E116.MirrorCS", {"start": v(-4.5, -201) * mm, "end": v(-22.5, -201) * mm, "construction": true});
            skPoint(sketch, "E117.MirrorP", {"position": v(-13.5, -201) * mm});
            skLineSegment(sketch, "E118.MirrorCS", {"start": v(-17, -183.5) * mm, "end": v(-10, -183.5) * mm});
            skLineSegment(sketch, "E119.MirrorCS", {"start": v(-4.5, -174) * mm, "end": v(-22.5, -174) * mm});
            skLineSegment(sketch, "E120.MirrorCS", {"start": v(-4.5, -228) * mm, "end": v(-22.5, -228) * mm});
            skLineSegment(sketch, "E121.MirrorCS", {"start": v(-17, -218.5) * mm, "end": v(-10, -218.5) * mm});
            skLineSegment(sketch, "E122.MirrorCS", {"start": v(-17, -183.5) * mm, "end": v(-17, -218.5) * mm});
            skLineSegment(sketch, "E123.MirrorCS", {"start": v(-10, -183.5) * mm, "end": v(-10, -218.5) * mm});
            skCircle(sketch, "E124", {"center": v(-13.5, -49) * mm, "radius": 3.25 * mm});
            skCircle(sketch, "E125.MirrorC", {"center": v(-13.5, -201) * mm, "radius": 3.25 * mm});
            skSolve(sketch);
        }
        {
            var Q0;
            Q0=makeQuery(id+"F30.imprint","IMPRINT",FACE,{"disambiguationData":[TD([[makeQuery(id+"F30.imprint","IMPRINT",EDGE,{"derivedFrom":sQuery(id+"F30.wireOp",EDGE,"E111.bottom")}),1.0]])]});
            var Q1;
            Q1=makeQuery(id+"F30.imprint","IMPRINT",FACE,{"disambiguationData":[TD([[makeQuery(id+"F30.imprint","IMPRINT",EDGE,{"derivedFrom":sQuery(id+"F30.wireOp",EDGE,"E118.MirrorCS")}),-1.0]])]});
            var Q2;
            Q2=makeQuery(id+"F30.imprint","IMPRINT",FACE,{"disambiguationData":[TD([[makeQuery(id+"F30.imprint","IMPRINT",EDGE,{"derivedFrom":sQuery(id+"F30.wireOp",EDGE,"E124")}),1.0]])]});
            var Q3;
            Q3=makeQuery(id+"F30.imprint","IMPRINT",FACE,{"disambiguationData":[TD([[makeQuery(id+"F30.imprint","IMPRINT",EDGE,{"derivedFrom":sQuery(id+"F30.wireOp",EDGE,"E125.MirrorC")}),-1.0]])]});
            extrude(context, id + "F31", {"entities" : qUnion([Q0, Q1, Q2, Q3]), "operationType" : NewBodyOperationType.REMOVE, "oppositeDirection" : true, "depth" : 47 * mm});
        }
        {
            var Q0;
            Q0=makeQuery(id+"F30.imprint","IMPRINT",FACE,{"disambiguationData":[TD([[makeQuery(id+"F30.imprint","IMPRINT",EDGE,{"derivedFrom":sQuery(id+"F30.wireOp",EDGE,"E114.MirrorCS")}),1.0]])]});
            var Q1;
            Q1=makeQuery(id+"F30.imprint","IMPRINT",FACE,{"disambiguationData":[TD([[makeQuery(id+"F30.imprint","IMPRINT",EDGE,{"derivedFrom":sQuery(id+"F30.wireOp",EDGE,"E107.bottom")}),1.0]])]});
            extrude(context, id + "F32", {"entities" : qUnion([Q0, Q1]), "operationType" : NewBodyOperationType.REMOVE, "oppositeDirection" : true, "depth" : 1 * mm});
        }
        {
            var Q0;
            Q0=makeQuery(id+"F30.imprint","IMPRINT",FACE,{"disambiguationData":[TD([[makeQuery(id+"F30.imprint","IMPRINT",EDGE,{"derivedFrom":sQuery(id+"F30.wireOp",EDGE,"E107.bottom")}),1.0]])]});
            var Q1;
            Q1=makeQuery(id+"F30.imprint","IMPRINT",FACE,{"disambiguationData":[TD([[makeQuery(id+"F30.imprint","IMPRINT",EDGE,{"derivedFrom":sQuery(id+"F30.wireOp",EDGE,"E111.bottom")}),1.0]])]});
            extrude(context, id + "F33", {"entities" : qUnion([Q0, Q1]), "oppositeDirection" : true, "depth" : 1 * mm});
        }
        {
            var Q0;
            Q0=makeQuery(id+"F30.imprint","IMPRINT",FACE,{"disambiguationData":[TD([[makeQuery(id+"F30.imprint","IMPRINT",EDGE,{"derivedFrom":sQuery(id+"F30.wireOp",EDGE,"E114.MirrorCS")}),1.0]])]});
            var Q1;
            Q1=makeQuery(id+"F30.imprint","IMPRINT",FACE,{"disambiguationData":[TD([[makeQuery(id+"F30.imprint","IMPRINT",EDGE,{"derivedFrom":sQuery(id+"F30.wireOp",EDGE,"E118.MirrorCS")}),-1.0]])]});
            extrude(context, id + "F34", {"entities" : qUnion([Q0, Q1]), "oppositeDirection" : true, "depth" : 1 * mm});
        }
        {
            var Q0;
            Q0=makeQuery(id+"F13.opExtrude","CAP_FACE",FACE,{"disambiguationData":[OSD([sQuery(id+"F10.wireOp",EDGE,"E62.MirrorCS"),sQuery(id+"F10.wireOp",EDGE,"E63.MirrorCS"),sQuery(id+"F10.wireOp",EDGE,"E64.MirrorCS"),sQuery(id+"F10.wireOp",EDGE,"E65.MirrorCS")])],"isStart":false});
            var sketch = newSketch(context, id + "F35", { "sketchPlane" : qUnion([Q0])});
            skLineSegment(sketch, "E126.0", {"start": v(212, 0.17) * mm, "end": v(212, -17.33) * mm});
            skLineSegment(sketch, "E126.1", {"start": v(212, 0.17) * mm, "end": v(190, 0.17) * mm});
            skLineSegment(sketch, "E126.2", {"start": v(190, 0.17) * mm, "end": v(190, -17.33) * mm});
            skLineSegment(sketch, "E126.3", {"start": v(212, -17.33) * mm, "end": v(190, -17.33) * mm});
            skLineSegment(sketch, "E127.0", {"start": v(218.4, 6.57) * mm, "end": v(218.4, -23.73) * mm});
            skLineSegment(sketch, "E127.1", {"start": v(218.4, 6.57) * mm, "end": v(204, 6.57) * mm});
            skLineSegment(sketch, "E127.2", {"start": v(183.6, 6.57) * mm, "end": v(183.6, -23.73) * mm});
            skLineSegment(sketch, "E127.3", {"start": v(218.4, -23.73) * mm, "end": v(183.6, -23.73) * mm});
            skLineSegment(sketch, "E128", {"start": v(201, 6.57) * mm, "end": v(201, 27.95) * mm, "construction": true});
            skLineSegment(sketch, "E129", {"start": v(198, 6.57) * mm, "end": v(198, 31.57) * mm});
            skLineSegment(sketch, "E130", {"start": v(198, 31.57) * mm, "end": v(204, 31.57) * mm});
            skLineSegment(sketch, "E131", {"start": v(204, 31.57) * mm, "end": v(204, 6.57) * mm});
            skLineSegment(sketch, "E132.trimOffspring", {"start": v(198, 6.57) * mm, "end": v(183.6, 6.57) * mm});
            skLineSegment(sketch, "E133", {"start": v(209.75, 6.57) * mm, "end": v(207.63, 18.57) * mm});
            skLineSegment(sketch, "E134", {"start": v(207.63, 18.57) * mm, "end": v(204, 18.57) * mm});
            skLineSegment(sketch, "E135.0", {"start": v(218.4, 34.57) * mm, "end": v(204, 34.57) * mm, "construction": true});
            skLineSegment(sketch, "E136.0", {"start": v(221, 31.57) * mm, "end": v(221, 6.57) * mm});
            skFitSpline(sketch, "E137", {"points": [v(207.63, 18.57) * mm, v(207.63, 21.56) * mm, v(208.68, 29.91) * mm, v(212.58, 33.42) * mm, v(216.05, 33.68) * mm, v(219.39, 31.81) * mm, v(221, 27.3) * mm, v(215.89, 20.8) * mm, v(211.98, 15.2) * mm, v(209.75, 6.57) * mm], "startDerivative": vector(-2.52, 31.56) * mm, "endDerivative": vector(-18.21, -86.7) * mm});
            skFitSpline(sketch, "E138.MirrorCS", {"points": [v(194.37, 18.57) * mm, v(194.37, 21.56) * mm, v(193.32, 29.91) * mm, v(189.42, 33.42) * mm, v(185.95, 33.68) * mm, v(182.61, 31.81) * mm, v(181, 27.3) * mm, v(186.11, 20.8) * mm, v(190.02, 15.2) * mm, v(192.25, 6.57) * mm], "startDerivative": vector(2.52, 31.56) * mm, "endDerivative": vector(18.21, -86.7) * mm});
            skLineSegment(sketch, "E139.MirrorCS", {"start": v(192.25, 6.57) * mm, "end": v(194.37, 18.57) * mm});
            skLineSegment(sketch, "E140.MirrorCS", {"start": v(194.37, 18.57) * mm, "end": v(198, 18.57) * mm});
            skSolve(sketch);
        }
        {
            var Q0;
            Q0=makeQuery(id+"F35.imprint","IMPRINT",FACE,{"disambiguationData":[TD([[makeQuery(id+"F35.imprint","IMPRINT",EDGE,{"derivedFrom":sQuery(id+"F35.wireOp",EDGE,"E126.0")}),1.0]])]});
            extrude(context, id + "F36", {"entities" : qUnion([Q0]), "depth" : 6 * mm});
        }
        {
            var Q0;
            Q0=makeQuery(id+"F36.opExtrude","CAP_EDGE",EDGE,{"disambiguationData":[OSD([sQuery(id+"F35.wireOp",EDGE,"E131")])],"isStart":false});
            var Q1;
            Q1=makeQuery(id+"F36.opExtrude","CAP_EDGE",EDGE,{"disambiguationData":[OSD([sQuery(id+"F35.wireOp",EDGE,"E131")])],"isStart":true});
            var Q2;
            Q2=makeQuery(id+"F36.opExtrude","CAP_EDGE",EDGE,{"disambiguationData":[OSD([sQuery(id+"F35.wireOp",EDGE,"E129")])],"isStart":false});
            var Q3;
            Q3=makeQuery(id+"F36.opExtrude","CAP_EDGE",EDGE,{"disambiguationData":[OSD([sQuery(id+"F35.wireOp",EDGE,"E129")])],"isStart":true});
            fillet(context, id + "F37", {"entities" : qUnion([Q0, Q1, Q2, Q3]), "radius" : 3 * mm, "tangentPropagation" : true, "allowEdgeOverflow" : false});
        }
        {
            var Q0;
            {var subQ3=sQuery(id+"F35.wireOp",EDGE,"E133");Q0=makeQuery(id+"F35.imprint","IMPRINT",FACE,{"disambiguationData":[TD([[makeQuery(id+"F35.imprint","IMPRINT",EDGE,{"derivedFrom":subQ3}),1.0]])]});}
            var Q1;
            Q1=sQuery(id+"F35.wireOp",EDGE,"E128");
            revolve(context, id + "F38", {"entities" : qUnion([Q0]), "axis" : qUnion([Q1]), "revolveType" : RevolveType.FULL});
        }
        {
            var Q0;
            {var subQ3=sQuery(id+"F35.wireOp",EDGE,"E133");Q0=makeQuery(id+"F35.imprint","IMPRINT",FACE,{"disambiguationData":[TD([[makeQuery(id+"F35.imprint","IMPRINT",EDGE,{"derivedFrom":subQ3}),1.0]])]});}
            var Q1;
            {var subQ0=sQuery(id+"F35.wireOp",EDGE,"E133");Q1=makeQuery(id+"F35.imprint","IMPRINT",FACE,{"disambiguationData":[TD([[makeQuery(id+"F35.imprint","IMPRINT",EDGE,{"derivedFrom":subQ0}),-1.0]])]});}
            var Q2;
            {var subQ4=sQuery(id+"F35.wireOp",EDGE,"E139.MirrorCS");Q2=makeQuery(id+"F35.imprint","IMPRINT",FACE,{"disambiguationData":[TD([[makeQuery(id+"F35.imprint","IMPRINT",EDGE,{"derivedFrom":subQ4}),-1.0]])]});}
            var Q3;
            Q3=makeQuery(id+"F35.imprint","IMPRINT",FACE,{"disambiguationData":[TD([[makeQuery(id+"F35.imprint","IMPRINT",EDGE,{"derivedFrom":sQuery(id+"F35.wireOp",EDGE,"E138.MirrorCS")}),1.0]])]});
            extrude(context, id + "F39", {"entities" : qUnion([Q0, Q1, Q2, Q3]), "operationType" : NewBodyOperationType.ADD, "depth" : 3.5 * mm, "symmetric" : true});
        }
    });
